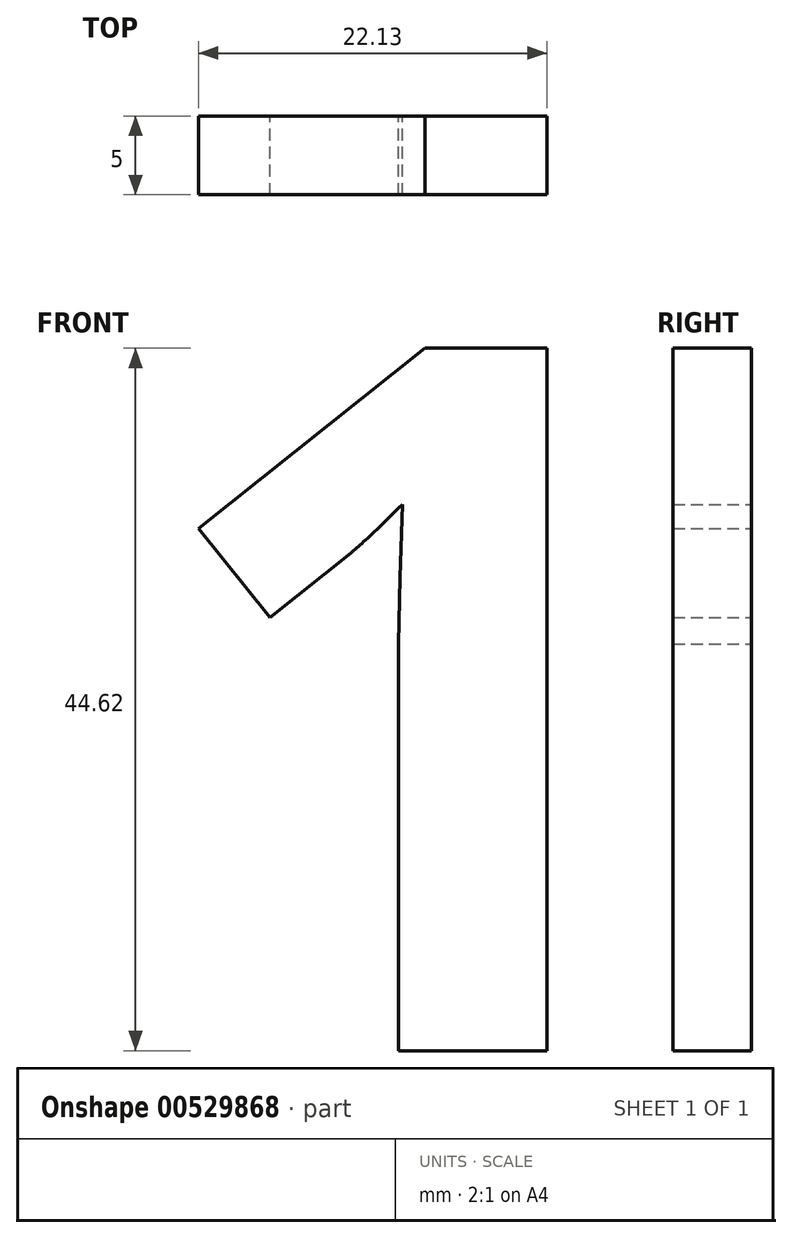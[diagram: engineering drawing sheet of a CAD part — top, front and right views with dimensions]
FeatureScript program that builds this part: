
annotation { "Feature Type Name" : "Feature", "Feature Type Description" : "" }
export const myFeature = defineFeature(function(context is Context, id is Id, definition is map)
    precondition{}
    {
        {
            var Q0;
            Q0=qCreatedBy(makeId("Front.planeOp"),FACE);
            var sketch = newSketch(context, id + "F0", { "sketchPlane" : qUnion([Q0])});
            skText(sketch, "E0", { "text": "1", "fontName": "OpenSans-Bold.ttf"});
            const initialGuessF0  = {"E0": [-0.05415, 0.00958, 1, 0, 0.045]};
            skSetInitialGuess(sketch, initialGuessF0);
            skSolve(sketch);
        }
        {
            var Q0;
            Q0=makeQuery(id+"F0.imprint","IMPRINT",FACE,{"disambiguationData":[TD([[makeQuery(id+"F0.imprint","IMPRINT",EDGE,{"derivedFrom":sQuery(id+"F0.wireOp",EDGE,"E0.sketch_text.stroke-0")}),-1.0]])]});
            extrude(context, id + "F1", {"entities" : qUnion([Q0]), "depth" : 5 * mm, "offsetDistance" : 25 * mm});
        }
    });
